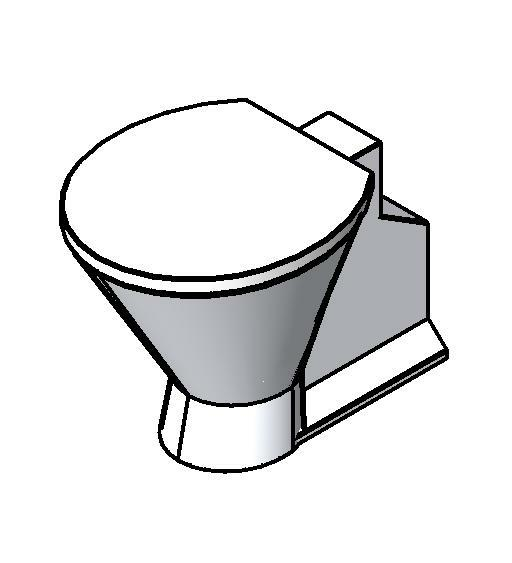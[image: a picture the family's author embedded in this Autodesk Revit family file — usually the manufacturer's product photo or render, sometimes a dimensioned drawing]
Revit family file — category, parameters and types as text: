
# Revit family: 23799-Deca_Acabamento para Registro de Gaveta 1 14 e 1 12 Grande Cromado_Gama_4900-13GD
name_source: partatom
category: Plumbing Fixtures
units: mm (PartAtom-declared; Revit-internal decimal feet)

## family parameters
Cut with Voids When Loaded = No
Host = Face
Part Type = Normal
Room Calculation Point = No
Round Connector Dimension = Use Radius
Shared = No

## types (1)
- 4900.C13.GD_CROMADO
    Acompanha o Produto = -
    Aprovado por = quattroD
    Atendimento ao Cliente = 0800 011 7073
    CWFU = 0
    Categoria = METAIS PARA BANHEIRO
    Composição Anel Vedação = -
    Composição Assento = -
    Composição Básica = Liga de Zinco(zamac),Plásticos de Engenharia
    Composição Componente = -
    Consumo = -
    Cor Interna = -
    Cor Principal = Cromado
    Cor Secundária = -
    Cores Componente = -
    Criado por = quattroD
    Código Pai = 4900.C13.GD
    Default Elevation = 1.8 m
    Description = ACABAMENTO P/ REGISTRO 1 1/4 E 1 1/2 GD GAMA -CROMADO
    Diâmetro Ponto de Esgoto = 0 m
    Diâmetro Água Fria = 0 m
    Informações Complementares = -
    Itens de Instalação = -
    Linha = Gama
    Manufacturer = Deca
    Material = Deca_Cromado
    Model = 4900.C13.GD
    Norma = Não Possui
    Peso Líquido (Kg) = 0.092
    Pressão máx. funcionamento = -
    Pressão mín. Aquec. Acúmulo = -
    Pressão mín. Aquec. Passagem = -
    Pressão mín. funcionamento = -
    Raio Ponto de Esgoto = 0 m
    Raio Água Fria = 0 m
    Saída de Esgoto = -
    Segmento = -
    Tipo de dispositivo economizador = -
    Tipo de mecanismo utilizado = -
    Tipo de rosca de entrada = -
    Tipo de rosca de saída = -
    URL = www.deca.com.br
    Vazão na Pressão máx. (L/min) = -
    Vazão na Pressão mín. (L/min) = -
    WFU = 0

## geometry (parser evidence)
native form markers: Sweep x2
no freeform markers — native parametric forms only
